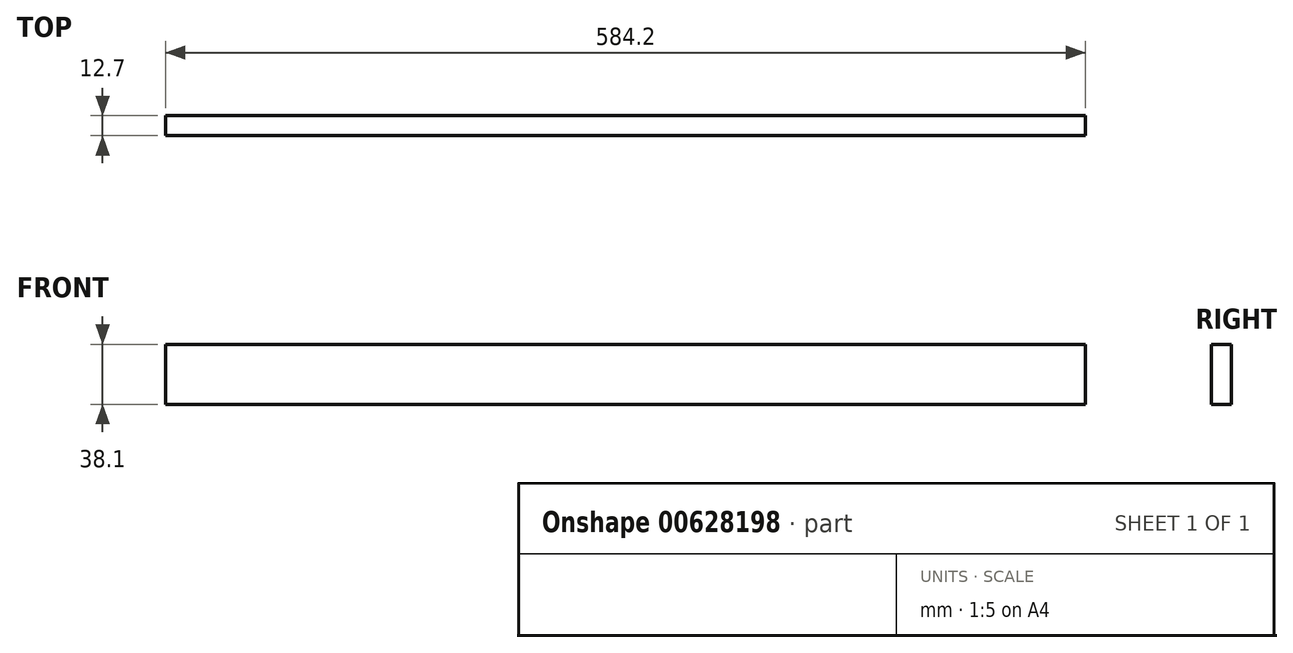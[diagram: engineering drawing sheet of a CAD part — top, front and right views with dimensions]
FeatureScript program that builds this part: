
annotation { "Feature Type Name" : "Feature", "Feature Type Description" : "" }
export const myFeature = defineFeature(function(context is Context, id is Id, definition is map)
    precondition{}
    {
        {
            var Q0;
            Q0=qCreatedBy(makeId("Front.planeOp"),FACE);
            var sketch = newSketch(context, id + "F0", { "sketchPlane" : qUnion([Q0])});
            skLineSegment(sketch, "E0.bottom", {"start": v(0, 0) * mm, "end": v(584.2, 0) * mm});
            skLineSegment(sketch, "E0.top", {"start": v(0, 38.1) * mm, "end": v(584.2, 38.1) * mm});
            skLineSegment(sketch, "E0.left", {"start": v(0, 0) * mm, "end": v(0, 38.1) * mm});
            skLineSegment(sketch, "E0.right", {"start": v(584.2, 0) * mm, "end": v(584.2, 38.1) * mm});
            skSolve(sketch);
        }
        {
            var Q0;
            Q0 = qSketchRegion(id + "F0", true);
            extrude(context, id + "F1", {"entities" : qUnion([Q0]), "depth" : 12.7 * mm, "offsetDistance" : 25.4 * mm});
        }
    });
